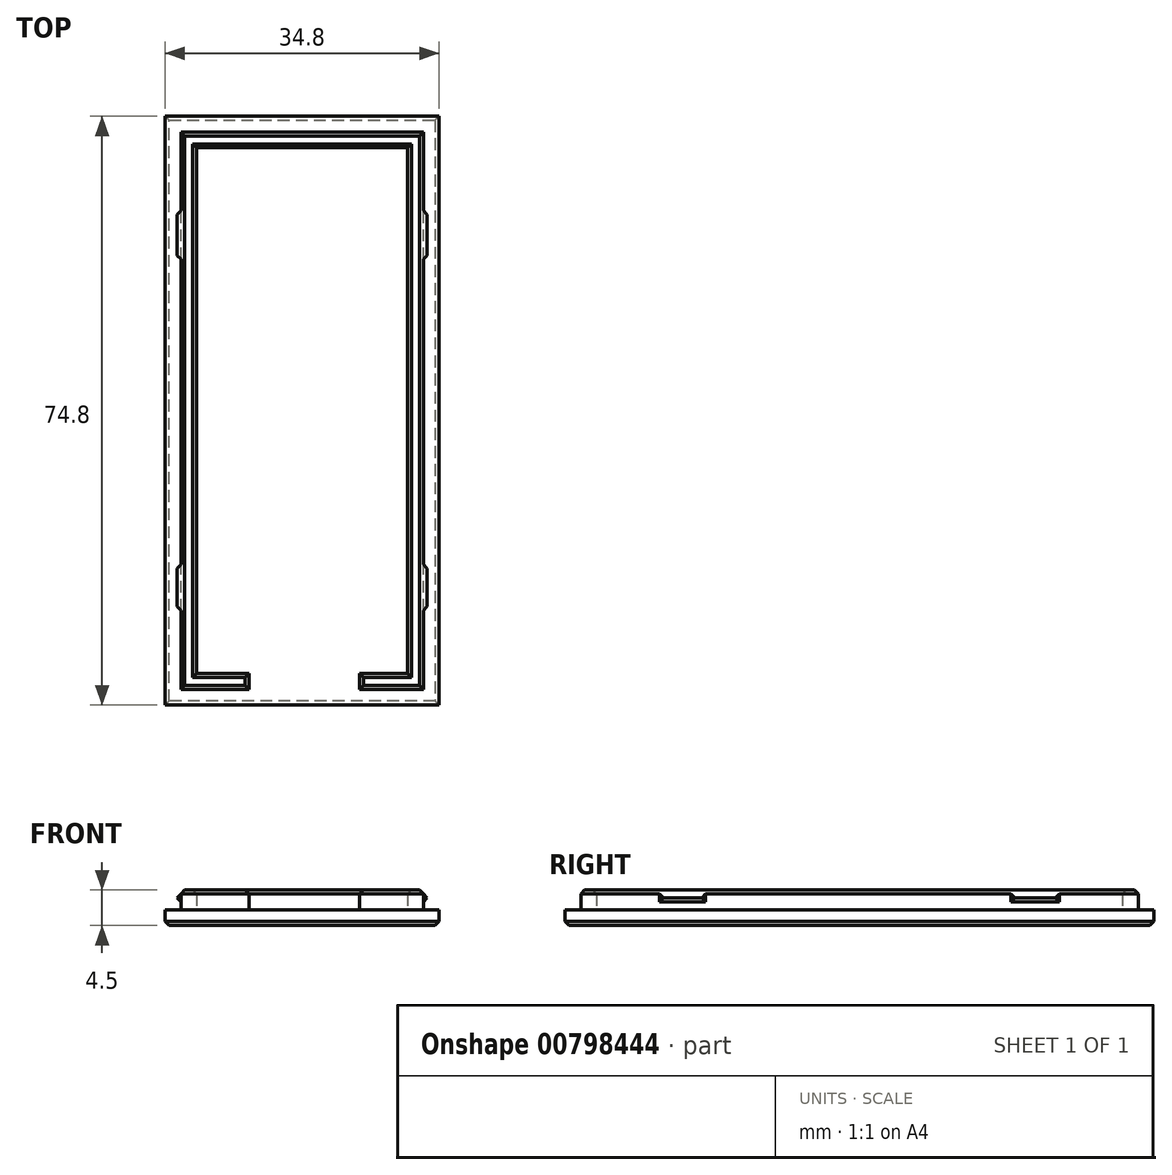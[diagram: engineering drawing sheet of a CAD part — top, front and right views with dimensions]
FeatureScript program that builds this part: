
annotation { "Feature Type Name" : "Feature", "Feature Type Description" : "" }
export const myFeature = defineFeature(function(context is Context, id is Id, definition is map)
    precondition{}
    {
        {
            var Q0;
            Q0=qCreatedBy(makeId("Top.planeOp"),FACE);
            var sketch = newSketch(context, id + "F0", { "sketchPlane" : qUnion([Q0])});
            skLineSegment(sketch, "E0.bottom", {"start": v(-20.5, 35.97) * mm, "end": v(20.3, 35.97) * mm});
            skLineSegment(sketch, "E0.top", {"start": v(-20.5, -24.83) * mm, "end": v(20.3, -24.83) * mm});
            skLineSegment(sketch, "E0.left", {"start": v(-20.5, 35.97) * mm, "end": v(-20.5, -24.83) * mm});
            skLineSegment(sketch, "E0.right", {"start": v(20.3, 35.97) * mm, "end": v(20.3, -24.83) * mm});
            skLineSegment(sketch, "E1.bottom", {"start": v(-22.5, 37.97) * mm, "end": v(22.3, 37.97) * mm});
            skLineSegment(sketch, "E1.top", {"start": v(-22.5, -26.83) * mm, "end": v(22.3, -26.83) * mm});
            skLineSegment(sketch, "E1.left", {"start": v(-22.5, 37.97) * mm, "end": v(-22.5, -26.83) * mm});
            skLineSegment(sketch, "E1.right", {"start": v(22.3, 37.97) * mm, "end": v(22.3, -26.83) * mm});
            skLineSegment(sketch, "E2.bottom", {"start": v(-21, -14.83) * mm, "end": v(21, -14.83) * mm});
            skLineSegment(sketch, "E2.top", {"start": v(-21, -8.96) * mm, "end": v(21, -8.96) * mm});
            skLineSegment(sketch, "E2.left", {"start": v(-21, -14.83) * mm, "end": v(-21, -8.96) * mm});
            skLineSegment(sketch, "E2.right", {"start": v(21, -14.83) * mm, "end": v(21, -8.96) * mm});
            skLineSegment(sketch, "E3.bottom", {"start": v(-21, 16.66) * mm, "end": v(20.8, 16.66) * mm});
            skLineSegment(sketch, "E3.top", {"start": v(-21, 25.97) * mm, "end": v(20.8, 25.97) * mm});
            skLineSegment(sketch, "E3.left", {"start": v(-21, 16.66) * mm, "end": v(-21, 25.97) * mm});
            skLineSegment(sketch, "E3.right", {"start": v(20.8, 16.66) * mm, "end": v(20.8, 25.97) * mm});
            skLineSegment(sketch, "E4.bottom", {"start": v(-17, -29.45) * mm, "end": v(17, -29.45) * mm});
            skLineSegment(sketch, "E4.top", {"start": v(-17, -24.83) * mm, "end": v(17, -24.83) * mm});
            skLineSegment(sketch, "E4.left", {"start": v(-17, -29.45) * mm, "end": v(-17, -24.83) * mm});
            skLineSegment(sketch, "E4.right", {"start": v(17, -29.45) * mm, "end": v(17, -24.83) * mm});
            skLineSegment(sketch, "E5.bottom", {"start": v(-7, -22.91) * mm, "end": v(7, -22.91) * mm});
            skLineSegment(sketch, "E5.top", {"start": v(-7, -32.6) * mm, "end": v(7, -32.6) * mm});
            skLineSegment(sketch, "E5.left", {"start": v(-7, -22.91) * mm, "end": v(-7, -32.6) * mm});
            skLineSegment(sketch, "E5.right", {"start": v(7, -22.91) * mm, "end": v(7, -32.6) * mm});
            skLineSegment(sketch, "E6", {"start": v(22.3, 37.97) * mm, "end": v(27.3, 37.97) * mm});
            skArc(sketch, "E7", {"start": v(27.3, 37.97) * mm, "mid": v(32.3, 32.97) * mm, "end": v(27.3, 27.97) * mm});
            skLineSegment(sketch, "E8", {"start": v(27.3, 27.97) * mm, "end": v(22.3, 25.09) * mm});
            skCircle(sketch, "E9", {"center": v(27.3, 32.97) * mm, "radius": 2.1 * mm});
            skLineSegment(sketch, "E10", {"start": v(-22.5, 37.97) * mm, "end": v(-27.5, 37.97) * mm});
            skArc(sketch, "E11", {"start": v(-27.5, 37.97) * mm, "mid": v(-32.5, 32.97) * mm, "end": v(-27.5, 27.97) * mm});
            skLineSegment(sketch, "E12", {"start": v(-27.5, 27.97) * mm, "end": v(-22.5, 25.09) * mm});
            skLineSegment(sketch, "E13", {"start": v(22.3, -26.83) * mm, "end": v(27.3, -26.83) * mm});
            skArc(sketch, "E14", {"start": v(27.3, -26.83) * mm, "mid": v(32.3, -21.83) * mm, "end": v(27.3, -16.83) * mm});
            skLineSegment(sketch, "E15", {"start": v(27.3, -16.83) * mm, "end": v(22.3, -13.94) * mm});
            skLineSegment(sketch, "E16", {"start": v(-22.5, -26.83) * mm, "end": v(-27.5, -26.83) * mm});
            skArc(sketch, "E17", {"start": v(-27.5, -26.83) * mm, "mid": v(-32.5, -21.83) * mm, "end": v(-27.5, -16.83) * mm});
            skLineSegment(sketch, "E18", {"start": v(-27.5, -16.83) * mm, "end": v(-22.5, -13.94) * mm});
            skCircle(sketch, "E19", {"center": v(-27.5, 32.97) * mm, "radius": 2.1 * mm});
            skCircle(sketch, "E20", {"center": v(-27.5, -21.83) * mm, "radius": 2.1 * mm});
            skCircle(sketch, "E21", {"center": v(27.3, -21.83) * mm, "radius": 2.1 * mm});
            skLineSegment(sketch, "E22.bottom", {"start": v(18.8, 34.47) * mm, "end": v(-19, 34.47) * mm});
            skLineSegment(sketch, "E22.top", {"start": v(18.8, -23.33) * mm, "end": v(-19, -23.33) * mm});
            skLineSegment(sketch, "E22.left", {"start": v(18.8, 34.47) * mm, "end": v(18.8, -23.33) * mm});
            skLineSegment(sketch, "E22.right", {"start": v(-19, 34.47) * mm, "end": v(-19, -23.33) * mm});
            skSolve(sketch);
        }
        {
            var Q0;
            Q0=qCreatedBy(makeId("Top.planeOp"),FACE);
            var sketch = newSketch(context, id + "F1", { "sketchPlane" : qUnion([Q0])});
            skLineSegment(sketch, "E23.bottom", {"start": v(-14.76, 37.75) * mm, "end": v(16.04, 37.75) * mm});
            skLineSegment(sketch, "E23.top", {"start": v(-14.76, -33.05) * mm, "end": v(16.04, -33.05) * mm});
            skLineSegment(sketch, "E23.left", {"start": v(-14.76, 37.75) * mm, "end": v(-14.76, -33.05) * mm});
            skLineSegment(sketch, "E23.right", {"start": v(16.04, 37.75) * mm, "end": v(16.04, -33.05) * mm});
            skLineSegment(sketch, "E24.bottom", {"start": v(-16.76, 39.75) * mm, "end": v(18.04, 39.75) * mm});
            skLineSegment(sketch, "E24.top", {"start": v(-16.76, -35.05) * mm, "end": v(18.04, -35.05) * mm});
            skLineSegment(sketch, "E24.left", {"start": v(-16.76, 39.75) * mm, "end": v(-16.76, -35.05) * mm});
            skLineSegment(sketch, "E24.right", {"start": v(18.04, 39.75) * mm, "end": v(18.04, -35.05) * mm});
            skLineSegment(sketch, "E25.bottom", {"start": v(-15.26, -23.05) * mm, "end": v(16.54, -23.05) * mm});
            skLineSegment(sketch, "E25.top", {"start": v(-15.26, -17.18) * mm, "end": v(16.54, -17.18) * mm});
            skLineSegment(sketch, "E25.left", {"start": v(-15.26, -23.05) * mm, "end": v(-15.26, -17.18) * mm});
            skLineSegment(sketch, "E25.right", {"start": v(16.54, -23.05) * mm, "end": v(16.54, -17.18) * mm});
            skLineSegment(sketch, "E26.bottom", {"start": v(-15.26, 21.59) * mm, "end": v(16.54, 21.59) * mm});
            skLineSegment(sketch, "E26.top", {"start": v(-15.26, 27.75) * mm, "end": v(16.54, 27.75) * mm});
            skLineSegment(sketch, "E26.left", {"start": v(-15.26, 21.59) * mm, "end": v(-15.26, 27.75) * mm});
            skLineSegment(sketch, "E26.right", {"start": v(16.54, 21.59) * mm, "end": v(16.54, 27.75) * mm});
            skLineSegment(sketch, "E27.left", {"start": v(-6.08, -31.05) * mm, "end": v(-6.08, -35.05) * mm});
            skLineSegment(sketch, "E27.right", {"start": v(7.92, -31.05) * mm, "end": v(7.92, -35.05) * mm});
            skLineSegment(sketch, "E28", {"start": v(-14.76, -26.05) * mm, "end": v(-16.76, -26.05) * mm});
            skLineSegment(sketch, "E29", {"start": v(-16.76, -3.25) * mm, "end": v(-14.76, -3.25) * mm});
            skLineSegment(sketch, "E30.bottom", {"start": v(-12.76, 35.75) * mm, "end": v(14.04, 35.75) * mm});
            skLineSegment(sketch, "E30.top", {"start": v(-12.76, -31.05) * mm, "end": v(14.04, -31.05) * mm});
            skLineSegment(sketch, "E30.left", {"start": v(-12.76, 35.75) * mm, "end": v(-12.76, -31.05) * mm});
            skLineSegment(sketch, "E30.right", {"start": v(14.04, 35.75) * mm, "end": v(14.04, -31.05) * mm});
            skSolve(sketch);
        }
        {
            var Q0;
            {var subQ6=sQuery(id+"F1.wireOp",EDGE,"E23.bottom");Q0=makeQuery(id+"F1.imprint","IMPRINT",FACE,{"disambiguationData":[TD([[makeQuery(id+"F1.imprint","IMPRINT",EDGE,{"derivedFrom":subQ6}),-1.0]])]});}
            var Q1;
            {var subQ1=sQuery(id+"F1.wireOp",EDGE,"E23.left");var subQ5=sQuery(id+"F1.wireOp",EDGE,"E23.top");var subQ6=makeQuery(id+"F1.imprint","INTERSECT",VERTEX,{"derivedFrom":[subQ5,subQ1]});Q1=makeQuery(id+"F1.imprint","IMPRINT",FACE,{"disambiguationData":[TD([[makeQuery(id+"F1.imprint","IMPRINT",EDGE,{"disambiguationData":[TD([[subQ6,-1.0]])],"derivedFrom":subQ5}),1.0]])]});}
            var Q2;
            {var subQ0=sQuery(id+"F1.wireOp",EDGE,"E26.top");var subQ1=sQuery(id+"F1.wireOp",EDGE,"E23.left");var subQ2=makeQuery(id+"F1.imprint","INTERSECT",VERTEX,{"derivedFrom":[subQ1,subQ0]});Q2=makeQuery(id+"F1.imprint","IMPRINT",FACE,{"disambiguationData":[TD([[makeQuery(id+"F1.imprint","IMPRINT",EDGE,{"disambiguationData":[TD([[subQ2,-1.0]])],"derivedFrom":subQ1}),1.0]])]});}
            var Q3;
            {var subQ0=sQuery(id+"F1.wireOp",EDGE,"E25.top");var subQ1=sQuery(id+"F1.wireOp",EDGE,"E23.left");var subQ2=makeQuery(id+"F1.imprint","INTERSECT",VERTEX,{"derivedFrom":[subQ1,subQ0]});Q3=makeQuery(id+"F1.imprint","IMPRINT",FACE,{"disambiguationData":[TD([[makeQuery(id+"F1.imprint","IMPRINT",EDGE,{"disambiguationData":[TD([[subQ2,-1.0]])],"derivedFrom":subQ1}),1.0]])]});}
            var Q4;
            {var subQ1=sQuery(id+"F1.wireOp",EDGE,"E23.left");var subQ8=makeQuery(id+"F1.imprint","INTERSECT",VERTEX,{"derivedFrom":[subQ1,sQuery(id+"F1.wireOp",EDGE,"E29")]});Q4=makeQuery(id+"F1.imprint","IMPRINT",FACE,{"disambiguationData":[TD([[makeQuery(id+"F1.imprint","IMPRINT",EDGE,{"disambiguationData":[TD([[subQ8,1.0]])],"derivedFrom":subQ1}),1.0]])]});}
            var Q5;
            {var subQ0=sQuery(id+"F1.wireOp",EDGE,"E26.bottom");var subQ1=sQuery(id+"F1.wireOp",EDGE,"E23.right");var subQ2=makeQuery(id+"F1.imprint","INTERSECT",VERTEX,{"derivedFrom":[subQ1,subQ0]});Q5=makeQuery(id+"F1.imprint","IMPRINT",FACE,{"disambiguationData":[TD([[makeQuery(id+"F1.imprint","IMPRINT",EDGE,{"disambiguationData":[TD([[subQ2,-1.0]])],"derivedFrom":subQ1}),-1.0]])]});}
            var Q6;
            {var subQ0=sQuery(id+"F1.wireOp",EDGE,"E25.top");var subQ1=sQuery(id+"F1.wireOp",EDGE,"E23.right");var subQ2=makeQuery(id+"F1.imprint","INTERSECT",VERTEX,{"derivedFrom":[subQ1,subQ0]});Q6=makeQuery(id+"F1.imprint","IMPRINT",FACE,{"disambiguationData":[TD([[makeQuery(id+"F1.imprint","IMPRINT",EDGE,{"disambiguationData":[TD([[subQ2,-1.0]])],"derivedFrom":subQ1}),-1.0]])]});}
            var Q7;
            {var subQ1=sQuery(id+"F1.wireOp",EDGE,"E23.right");var subQ8=sQuery(id+"F1.wireOp",EDGE,"E23.top");var subQ10=makeQuery(id+"F1.imprint","INTERSECT",VERTEX,{"derivedFrom":[subQ8,subQ1]});Q7=makeQuery(id+"F1.imprint","IMPRINT",FACE,{"disambiguationData":[TD([[makeQuery(id+"F1.imprint","IMPRINT",EDGE,{"disambiguationData":[TD([[subQ10,1.0]])],"derivedFrom":subQ8}),1.0]])]});}
            var Q8;
            {var subQ0=sQuery(id+"F1.wireOp",EDGE,"E26.top");var subQ1=sQuery(id+"F1.wireOp",EDGE,"E23.right");var subQ2=makeQuery(id+"F1.imprint","INTERSECT",VERTEX,{"derivedFrom":[subQ1,subQ0]});Q8=makeQuery(id+"F1.imprint","IMPRINT",FACE,{"disambiguationData":[TD([[makeQuery(id+"F1.imprint","IMPRINT",EDGE,{"disambiguationData":[TD([[subQ2,-1.0]])],"derivedFrom":subQ1}),-1.0]])]});}
            var Q9;
            {var subQ3=sQuery(id+"F1.wireOp",EDGE,"E28");Q9=makeQuery(id+"F1.imprint","IMPRINT",FACE,{"disambiguationData":[TD([[makeQuery(id+"F1.imprint","IMPRINT",EDGE,{"derivedFrom":subQ3}),1.0]])]});}
            var Q10;
            {var subQ0=sQuery(id+"F1.wireOp",EDGE,"E27.left");var subQ1=sQuery(id+"F1.wireOp",EDGE,"E23.top");var subQ2=makeQuery(id+"F1.imprint","INTERSECT",VERTEX,{"derivedFrom":[subQ1,subQ0]});Q10=makeQuery(id+"F1.imprint","IMPRINT",FACE,{"disambiguationData":[TD([[makeQuery(id+"F1.imprint","IMPRINT",EDGE,{"disambiguationData":[TD([[subQ2,-1.0]])],"derivedFrom":subQ1}),1.0]])]});}
            var Q11;
            {var subQ0=sQuery(id+"F1.wireOp",EDGE,"E27.left");var subQ1=sQuery(id+"F1.wireOp",EDGE,"E23.top");var subQ2=makeQuery(id+"F1.imprint","INTERSECT",VERTEX,{"derivedFrom":[subQ1,subQ0]});Q11=makeQuery(id+"F1.imprint","IMPRINT",FACE,{"disambiguationData":[TD([[makeQuery(id+"F1.imprint","IMPRINT",EDGE,{"disambiguationData":[TD([[subQ2,-1.0]])],"derivedFrom":subQ1}),-1.0]])]});}
            var Q12;
            {var subQ0=sQuery(id+"F1.wireOp",EDGE,"E30.left");var subQ1=sQuery(id+"F1.wireOp",EDGE,"E26.bottom");var subQ2=makeQuery(id+"F1.imprint","INTERSECT",VERTEX,{"derivedFrom":[subQ1,subQ0]});Q12=makeQuery(id+"F1.imprint","IMPRINT",FACE,{"disambiguationData":[TD([[makeQuery(id+"F1.imprint","IMPRINT",EDGE,{"disambiguationData":[TD([[subQ2,-1.0]])],"derivedFrom":subQ1}),1.0]])]});}
            var Q13;
            {var subQ0=sQuery(id+"F1.wireOp",EDGE,"E30.left");var subQ1=sQuery(id+"F1.wireOp",EDGE,"E25.top");var subQ2=makeQuery(id+"F1.imprint","INTERSECT",VERTEX,{"derivedFrom":[subQ1,subQ0]});Q13=makeQuery(id+"F1.imprint","IMPRINT",FACE,{"disambiguationData":[TD([[makeQuery(id+"F1.imprint","IMPRINT",EDGE,{"disambiguationData":[TD([[subQ2,-1.0]])],"derivedFrom":subQ1}),1.0]])]});}
            var Q14;
            {var subQ5=sQuery(id+"F1.wireOp",EDGE,"E30.left");var subQ7=sQuery(id+"F1.wireOp",EDGE,"E25.bottom");var subQ9=makeQuery(id+"F1.imprint","INTERSECT",VERTEX,{"derivedFrom":[subQ7,subQ5]});Q14=makeQuery(id+"F1.imprint","IMPRINT",FACE,{"disambiguationData":[TD([[makeQuery(id+"F1.imprint","IMPRINT",EDGE,{"disambiguationData":[TD([[subQ9,-1.0]])],"derivedFrom":subQ7}),-1.0]])]});}
            var Q15;
            {var subQ15=sQuery(id+"F1.wireOp",EDGE,"E23.bottom");Q15=makeQuery(id+"F1.imprint","IMPRINT",FACE,{"disambiguationData":[TD([[makeQuery(id+"F1.imprint","IMPRINT",EDGE,{"derivedFrom":subQ15}),1.0]])]});}
            var Q16;
            {var subQ5=sQuery(id+"F1.wireOp",EDGE,"E30.bottom");Q16=makeQuery(id+"F1.imprint","IMPRINT",FACE,{"disambiguationData":[TD([[makeQuery(id+"F1.imprint","IMPRINT",EDGE,{"derivedFrom":subQ5}),-1.0]])]});}
            var Q17;
            {var subQ3=sQuery(id+"F1.wireOp",EDGE,"E25.left");Q17=makeQuery(id+"F1.imprint","IMPRINT",FACE,{"disambiguationData":[TD([[makeQuery(id+"F1.imprint","IMPRINT",EDGE,{"derivedFrom":subQ3}),1.0]])]});}
            var Q18;
            {var subQ0=sQuery(id+"F1.wireOp",EDGE,"E30.left");var subQ1=sQuery(id+"F1.wireOp",EDGE,"E25.bottom");var subQ2=makeQuery(id+"F1.imprint","INTERSECT",VERTEX,{"derivedFrom":[subQ1,subQ0]});Q18=makeQuery(id+"F1.imprint","IMPRINT",FACE,{"disambiguationData":[TD([[makeQuery(id+"F1.imprint","IMPRINT",EDGE,{"disambiguationData":[TD([[subQ2,-1.0]])],"derivedFrom":subQ1}),1.0]])]});}
            var Q19;
            {var subQ5=sQuery(id+"F1.wireOp",EDGE,"E25.left");Q19=makeQuery(id+"F1.imprint","IMPRINT",FACE,{"disambiguationData":[TD([[makeQuery(id+"F1.imprint","IMPRINT",EDGE,{"derivedFrom":subQ5}),-1.0]])]});}
            var Q20;
            {var subQ5=sQuery(id+"F1.wireOp",EDGE,"E26.left");Q20=makeQuery(id+"F1.imprint","IMPRINT",FACE,{"disambiguationData":[TD([[makeQuery(id+"F1.imprint","IMPRINT",EDGE,{"derivedFrom":subQ5}),-1.0]])]});}
            var Q21;
            {var subQ5=sQuery(id+"F1.wireOp",EDGE,"E25.right");Q21=makeQuery(id+"F1.imprint","IMPRINT",FACE,{"disambiguationData":[TD([[makeQuery(id+"F1.imprint","IMPRINT",EDGE,{"derivedFrom":subQ5}),1.0]])]});}
            var Q22;
            {var subQ5=sQuery(id+"F1.wireOp",EDGE,"E26.right");Q22=makeQuery(id+"F1.imprint","IMPRINT",FACE,{"disambiguationData":[TD([[makeQuery(id+"F1.imprint","IMPRINT",EDGE,{"derivedFrom":subQ5}),1.0]])]});}
            extrude(context, id + "F2", {"entities" : qUnion([Q0, Q1, Q2, Q3, Q4, Q5, Q6, Q7, Q8, Q9, Q10, Q11, Q12, Q13, Q14, Q15, Q16, Q17, Q18, Q19, Q20, Q21, Q22]), "depth" : 2 * mm, "offsetDistance" : 25 * mm});
        }
        {
            var Q0;
            {var subQ6=sQuery(id+"F1.wireOp",EDGE,"E23.bottom");Q0=makeQuery(id+"F1.imprint","IMPRINT",FACE,{"disambiguationData":[TD([[makeQuery(id+"F1.imprint","IMPRINT",EDGE,{"derivedFrom":subQ6}),-1.0]])]});}
            var Q1;
            {var subQ0=sQuery(id+"F1.wireOp",EDGE,"E26.top");var subQ1=sQuery(id+"F1.wireOp",EDGE,"E23.left");var subQ2=makeQuery(id+"F1.imprint","INTERSECT",VERTEX,{"derivedFrom":[subQ1,subQ0]});Q1=makeQuery(id+"F1.imprint","IMPRINT",FACE,{"disambiguationData":[TD([[makeQuery(id+"F1.imprint","IMPRINT",EDGE,{"disambiguationData":[TD([[subQ2,-1.0]])],"derivedFrom":subQ1}),1.0]])]});}
            var Q2;
            {var subQ0=sQuery(id+"F1.wireOp",EDGE,"E26.top");var subQ1=sQuery(id+"F1.wireOp",EDGE,"E23.right");var subQ2=makeQuery(id+"F1.imprint","INTERSECT",VERTEX,{"derivedFrom":[subQ1,subQ0]});Q2=makeQuery(id+"F1.imprint","IMPRINT",FACE,{"disambiguationData":[TD([[makeQuery(id+"F1.imprint","IMPRINT",EDGE,{"disambiguationData":[TD([[subQ2,-1.0]])],"derivedFrom":subQ1}),-1.0]])]});}
            var Q3;
            {var subQ0=sQuery(id+"F1.wireOp",EDGE,"E26.bottom");var subQ1=sQuery(id+"F1.wireOp",EDGE,"E23.right");var subQ2=makeQuery(id+"F1.imprint","INTERSECT",VERTEX,{"derivedFrom":[subQ1,subQ0]});Q3=makeQuery(id+"F1.imprint","IMPRINT",FACE,{"disambiguationData":[TD([[makeQuery(id+"F1.imprint","IMPRINT",EDGE,{"disambiguationData":[TD([[subQ2,-1.0]])],"derivedFrom":subQ1}),-1.0]])]});}
            var Q4;
            {var subQ1=sQuery(id+"F1.wireOp",EDGE,"E23.left");var subQ8=makeQuery(id+"F1.imprint","INTERSECT",VERTEX,{"derivedFrom":[subQ1,sQuery(id+"F1.wireOp",EDGE,"E29")]});Q4=makeQuery(id+"F1.imprint","IMPRINT",FACE,{"disambiguationData":[TD([[makeQuery(id+"F1.imprint","IMPRINT",EDGE,{"disambiguationData":[TD([[subQ8,1.0]])],"derivedFrom":subQ1}),1.0]])]});}
            var Q5;
            {var subQ0=sQuery(id+"F1.wireOp",EDGE,"E25.top");var subQ1=sQuery(id+"F1.wireOp",EDGE,"E23.right");var subQ2=makeQuery(id+"F1.imprint","INTERSECT",VERTEX,{"derivedFrom":[subQ1,subQ0]});Q5=makeQuery(id+"F1.imprint","IMPRINT",FACE,{"disambiguationData":[TD([[makeQuery(id+"F1.imprint","IMPRINT",EDGE,{"disambiguationData":[TD([[subQ2,-1.0]])],"derivedFrom":subQ1}),-1.0]])]});}
            var Q6;
            {var subQ1=sQuery(id+"F1.wireOp",EDGE,"E23.right");var subQ8=sQuery(id+"F1.wireOp",EDGE,"E23.top");var subQ10=makeQuery(id+"F1.imprint","INTERSECT",VERTEX,{"derivedFrom":[subQ8,subQ1]});Q6=makeQuery(id+"F1.imprint","IMPRINT",FACE,{"disambiguationData":[TD([[makeQuery(id+"F1.imprint","IMPRINT",EDGE,{"disambiguationData":[TD([[subQ10,1.0]])],"derivedFrom":subQ8}),1.0]])]});}
            var Q7;
            {var subQ1=sQuery(id+"F1.wireOp",EDGE,"E23.left");var subQ5=sQuery(id+"F1.wireOp",EDGE,"E23.top");var subQ6=makeQuery(id+"F1.imprint","INTERSECT",VERTEX,{"derivedFrom":[subQ5,subQ1]});Q7=makeQuery(id+"F1.imprint","IMPRINT",FACE,{"disambiguationData":[TD([[makeQuery(id+"F1.imprint","IMPRINT",EDGE,{"disambiguationData":[TD([[subQ6,-1.0]])],"derivedFrom":subQ5}),1.0]])]});}
            var Q8;
            {var subQ0=sQuery(id+"F1.wireOp",EDGE,"E25.top");var subQ1=sQuery(id+"F1.wireOp",EDGE,"E23.left");var subQ2=makeQuery(id+"F1.imprint","INTERSECT",VERTEX,{"derivedFrom":[subQ1,subQ0]});Q8=makeQuery(id+"F1.imprint","IMPRINT",FACE,{"disambiguationData":[TD([[makeQuery(id+"F1.imprint","IMPRINT",EDGE,{"disambiguationData":[TD([[subQ2,-1.0]])],"derivedFrom":subQ1}),1.0]])]});}
            extrude(context, id + "F3", {"entities" : qUnion([Q0, Q1, Q2, Q3, Q4, Q5, Q6, Q7, Q8]), "operationType" : NewBodyOperationType.ADD, "depth" : 4.5 * mm, "offsetDistance" : 25 * mm, "hasSecondDirection" : true, "secondDirectionOppositeDirection" : false, "secondDirectionDepth" : 1 * mm});
        }
        {
            var Q0;
            {var subQ5=sQuery(id+"F1.wireOp",EDGE,"E26.left");Q0=makeQuery(id+"F1.imprint","IMPRINT",FACE,{"disambiguationData":[TD([[makeQuery(id+"F1.imprint","IMPRINT",EDGE,{"derivedFrom":subQ5}),-1.0]])]});}
            var Q1;
            {var subQ5=sQuery(id+"F1.wireOp",EDGE,"E25.left");Q1=makeQuery(id+"F1.imprint","IMPRINT",FACE,{"disambiguationData":[TD([[makeQuery(id+"F1.imprint","IMPRINT",EDGE,{"derivedFrom":subQ5}),-1.0]])]});}
            var Q2;
            {var subQ5=sQuery(id+"F1.wireOp",EDGE,"E25.right");Q2=makeQuery(id+"F1.imprint","IMPRINT",FACE,{"disambiguationData":[TD([[makeQuery(id+"F1.imprint","IMPRINT",EDGE,{"derivedFrom":subQ5}),1.0]])]});}
            var Q3;
            {var subQ5=sQuery(id+"F1.wireOp",EDGE,"E26.right");Q3=makeQuery(id+"F1.imprint","IMPRINT",FACE,{"disambiguationData":[TD([[makeQuery(id+"F1.imprint","IMPRINT",EDGE,{"derivedFrom":subQ5}),1.0]])]});}
            extrude(context, id + "F4", {"entities" : qUnion([Q0, Q1, Q2, Q3]), "operationType" : NewBodyOperationType.ADD, "depth" : 4 * mm, "offsetDistance" : 25 * mm, "hasSecondDirection" : true, "secondDirectionOppositeDirection" : false, "secondDirectionDepth" : 3 * mm});
        }
        {
            var Q0;
            Q0=makeQuery(id+"F2.opExtrude","CAP_FACE",FACE,{"disambiguationData":[OSD([sQuery(id+"F1.wireOp",EDGE,"E24.bottom"),sQuery(id+"F1.wireOp",EDGE,"E24.top"),sQuery(id+"F1.wireOp",EDGE,"E24.left"),sQuery(id+"F1.wireOp",EDGE,"E24.right")])],"isStart":true});
            var Q1;
            Q1=makeQuery(id+"F4.opExtrude","SWEPT_FACE",FACE,{"disambiguationData":[OSD([sQuery(id+"F1.wireOp",EDGE,"E25.right")])]});
            var Q2;
            Q2=makeQuery(id+"F4.opExtrude","SWEPT_FACE",FACE,{"disambiguationData":[OSD([sQuery(id+"F1.wireOp",EDGE,"E26.right")])]});
            var Q3;
            Q3=makeQuery(id+"F4.opExtrude","SWEPT_FACE",FACE,{"disambiguationData":[OSD([sQuery(id+"F1.wireOp",EDGE,"E26.left")])]});
            var Q4;
            Q4=makeQuery(id+"F4.opExtrude","SWEPT_FACE",FACE,{"disambiguationData":[OSD([sQuery(id+"F1.wireOp",EDGE,"E25.left")])]});
            var Q5;
            Q5=makeQuery(id+"F3.opExtrude","CAP_FACE",FACE,{"disambiguationData":[OSD([sQuery(id+"F1.wireOp",EDGE,"E23.bottom"),sQuery(id+"F1.wireOp",EDGE,"E23.top"),sQuery(id+"F1.wireOp",EDGE,"E23.left"),sQuery(id+"F1.wireOp",EDGE,"E23.right"),sQuery(id+"F1.wireOp",EDGE,"E27.left"),sQuery(id+"F1.wireOp",EDGE,"E27.right"),sQuery(id+"F1.wireOp",EDGE,"E30.bottom"),sQuery(id+"F1.wireOp",EDGE,"E30.top"),sQuery(id+"F1.wireOp",EDGE,"E30.left"),sQuery(id+"F1.wireOp",EDGE,"E30.right")])],"isStart":false});
            chamfer(context, id + "F5", {"entities" : qUnion([Q0, Q1, Q2, Q3, Q4, Q5]), "width" : 0.5 * mm, "tangentPropagation" : true});
        }
    });
